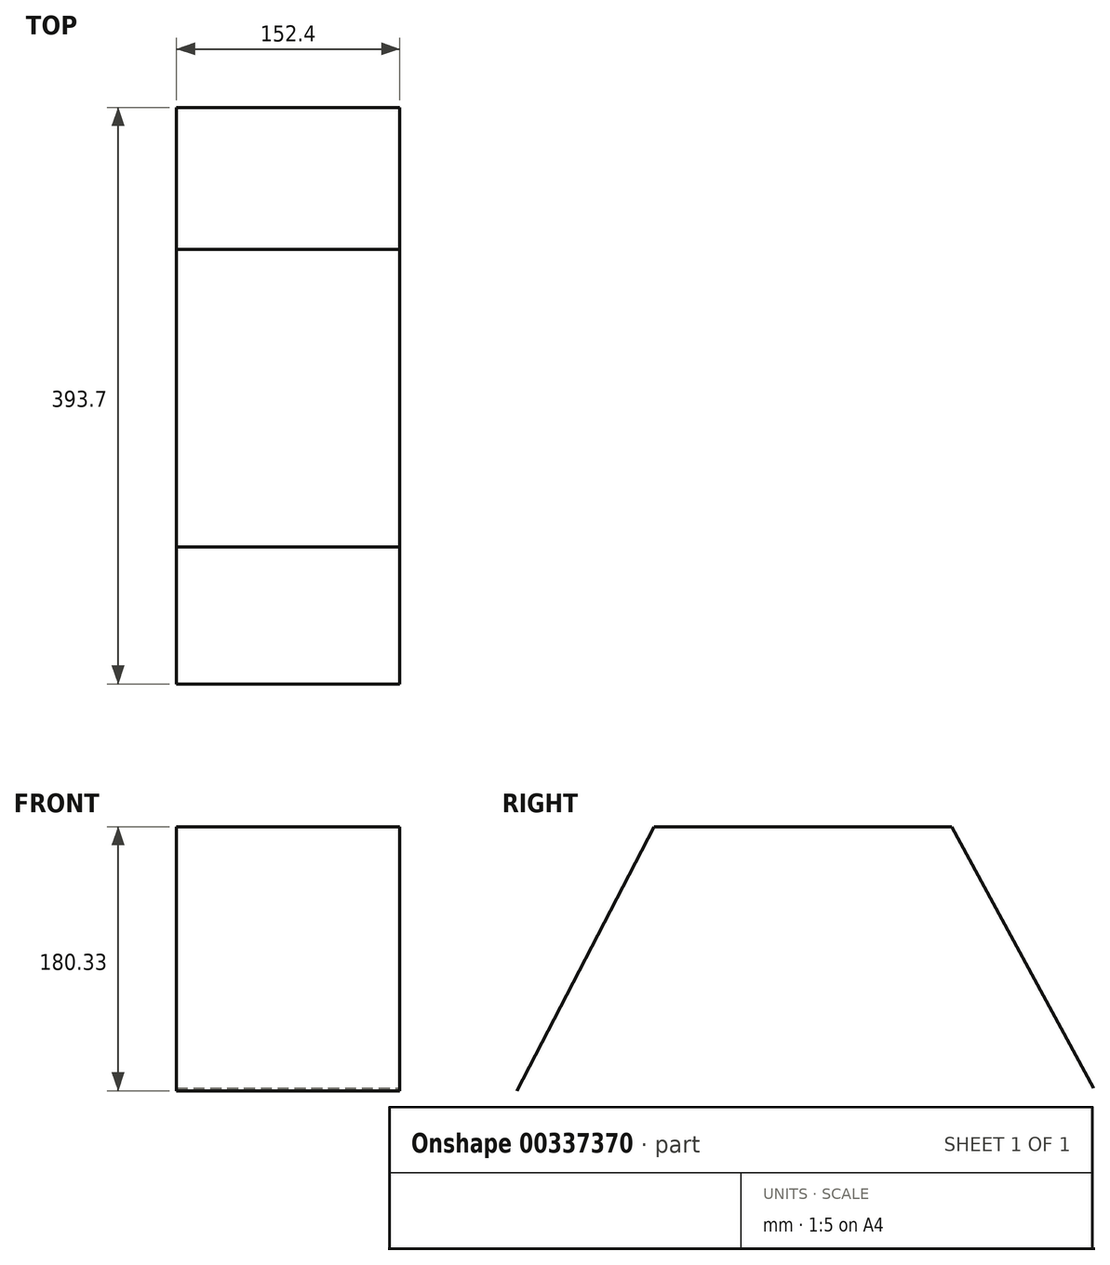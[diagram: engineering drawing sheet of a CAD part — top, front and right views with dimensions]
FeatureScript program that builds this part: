
annotation { "Feature Type Name" : "Feature", "Feature Type Description" : "" }
export const myFeature = defineFeature(function(context is Context, id is Id, definition is map)
    precondition{}
    {
        {
            var Q0;
            Q0=qCreatedBy(makeId("Right.planeOp"),FACE);
            var sketch = newSketch(context, id + "F0", { "sketchPlane" : qUnion([Q0])});
            skLineSegment(sketch, "E0", {"start": v(-113.58, 24.9) * mm, "end": v(89.62, 24.9) * mm});
            skLineSegment(sketch, "E1", {"start": v(89.62, 24.9) * mm, "end": v(186.47, -153.73) * mm});
            skLineSegment(sketch, "E2", {"start": v(-113.58, 24.9) * mm, "end": v(-207.23, -155.43) * mm});
            skSolve(sketch);
        }
        {
            var Q0;
            Q0 = qSketchRegion(id + "F0", true);
            var Q1;
            Q1=sQuery(id+"F0.wireOp",EDGE,"E0");
            var Q2;
            Q2=sQuery(id+"F0.wireOp",EDGE,"E1");
            var Q3;
            Q3=sQuery(id+"F0.wireOp",EDGE,"E2");
            extrude(context, id + "F1", {"entities" : qUnion([Q0]), "bodyType" : ToolBodyType.SURFACE, "surfaceEntities" : qUnion([Q1, Q2, Q3]), "depth" : 152.4 * mm});
        }
    });
